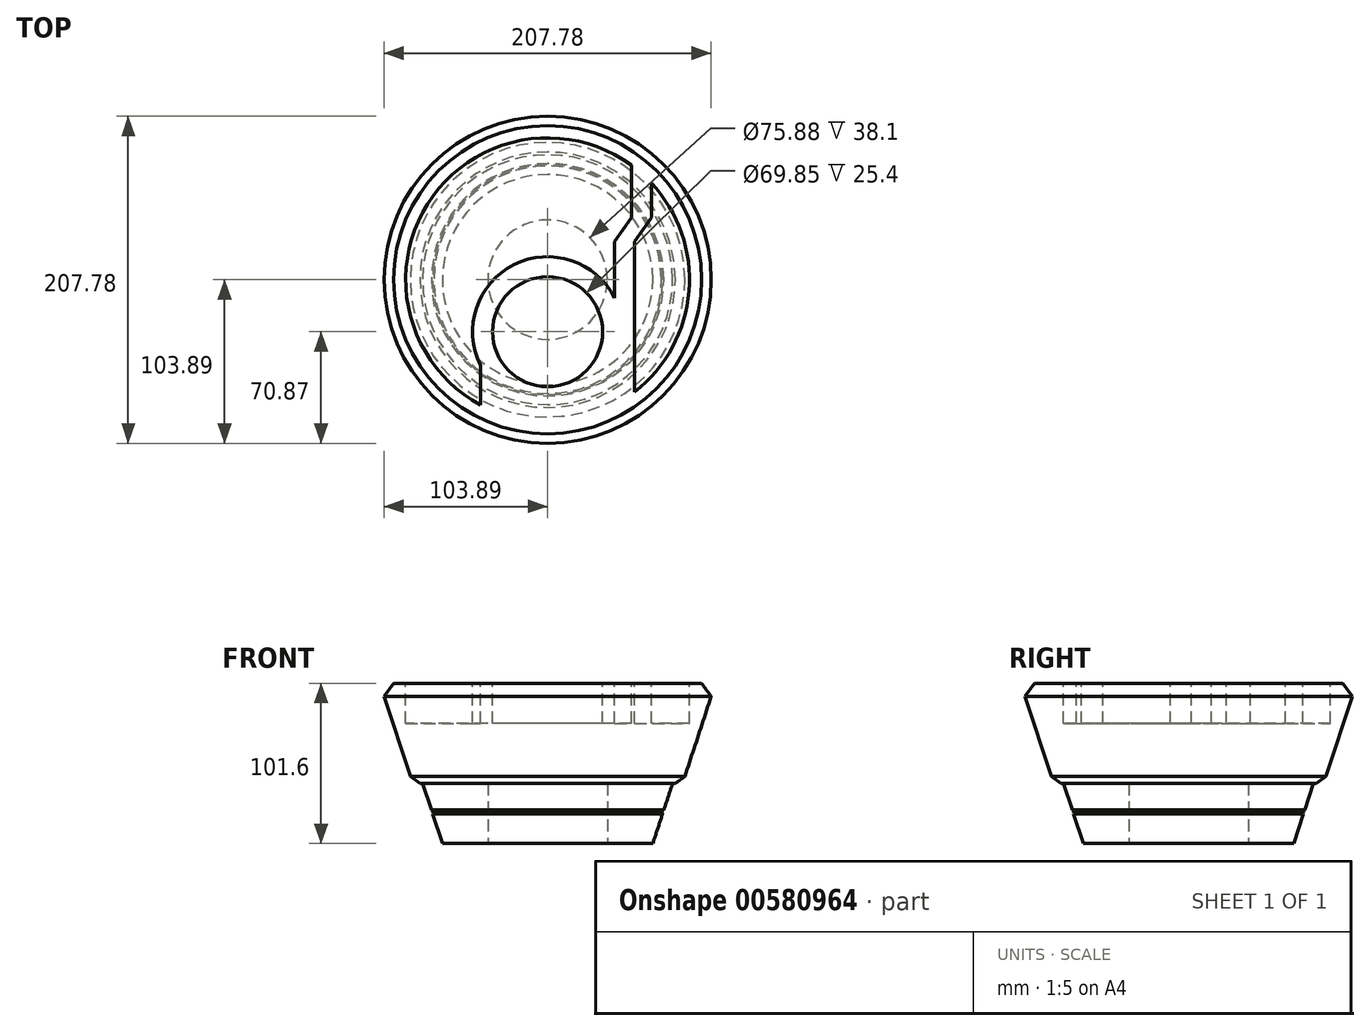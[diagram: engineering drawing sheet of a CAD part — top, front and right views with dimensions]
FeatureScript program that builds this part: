
annotation { "Feature Type Name" : "Feature", "Feature Type Description" : "" }
export const myFeature = defineFeature(function(context is Context, id is Id, definition is map)
    precondition{}
    {
        {
            var Q0;
            Q0=qCreatedBy(makeId("Top.planeOp"),FACE);
            var sketch = newSketch(context, id + "F0", { "sketchPlane" : qUnion([Q0])});
            skCircle(sketch, "E0", {"center": v(0, 0) * mm, "radius": 66.85 * mm});
            skSolve(sketch);
        }
        {
            var Q0;
            Q0=qCreatedBy(makeId("Top.planeOp"),FACE);
            cPlane(context, id + "F1", {"entities" : qUnion([Q0]), "cplaneType" : CPlaneType.OFFSET, "offset" : 101.6 * mm, "width" : 152.4 * mm, "height" : 152.4 * mm});
        }
        {
            var Q0;
            Q0=qCreatedBy(id+"F1.planeOp",FACE);
            var sketch = newSketch(context, id + "F2", { "sketchPlane" : qUnion([Q0])});
            skCircle(sketch, "E1", {"center": v(0, 0) * mm, "radius": 100.28 * mm});
            skSolve(sketch);
        }
        {
            var Q0;
            Q0=makeQuery(id+"F2.imprint","IMPRINT",FACE,{"disambiguationData":[TD([[makeQuery(id+"F2.imprint","IMPRINT",EDGE,{"derivedFrom":sQuery(id+"F2.wireOp",EDGE,"E1")}),1.0]])]});
            var Q1;
            Q1=makeQuery(id+"F0.imprint","IMPRINT",FACE,{"disambiguationData":[TD([[makeQuery(id+"F0.imprint","IMPRINT",EDGE,{"derivedFrom":sQuery(id+"F0.wireOp",EDGE,"E0")}),1.0]])]});
            var Q2;
            Q2=sQuery(id+"F2.wireOp",EDGE,"Eyu8YDiN-lEGU-Wuxt-0ncA-RZLAWeJK4OgB");
            var Q3;
            Q3=sQuery(id+"F0.wireOp",EDGE,"fgfE4CqQ-t5n6-ucAx-yhIW-5wF2yx0Jya2k");
            loft(context, id + "F3", {"sheetProfilesArray" : [{ "sheetProfileEntities" : qUnion([Q0]) }, { "sheetProfileEntities" : qUnion([Q1]) }], "wireProfilesArray" : [{ "wireProfileEntities" : qUnion([Q2]) }, { "wireProfileEntities" : qUnion([Q3]) }]});
        }
        {
            var Q0;
            Q0=qCreatedBy(makeId("Top.planeOp"),FACE);
            var sketch = newSketch(context, id + "F4", { "sketchPlane" : qUnion([Q0])});
            skCircle(sketch, "E2", {"center": v(0, 0) * mm, "radius": 37.94 * mm});
            skSolve(sketch);
        }
        {
            var Q0;
            Q0=makeQuery(id+"F4.imprint","IMPRINT",FACE,{"disambiguationData":[TD([[makeQuery(id+"F4.imprint","IMPRINT",EDGE,{"derivedFrom":sQuery(id+"F4.wireOp",EDGE,"E2")}),1.0]])]});
            extrude(context, id + "F5", {"entities" : qUnion([Q0]), "operationType" : NewBodyOperationType.REMOVE, "depth" : 53.34 * mm, "offsetDistance" : 25.4 * mm});
        }
        {
            var Q0;
            Q0=qCreatedBy(makeId("Top.planeOp"),FACE);
            cPlane(context, id + "F6", {"entities" : qUnion([Q0]), "cplaneType" : CPlaneType.OFFSET, "offset" : 38.1 * mm, "width" : 152.4 * mm, "height" : 152.4 * mm});
        }
        {
            var Q0;
            Q0=qCreatedBy(id+"F6.planeOp",FACE);
            var sketch = newSketch(context, id + "F7", { "sketchPlane" : qUnion([Q0])});
            skCircle(sketch, "E3", {"center": v(0, 0) * mm, "radius": 85.73 * mm});
            skSolve(sketch);
        }
        {
            var Q0;
            Q0=qCreatedBy(id+"F1.planeOp",FACE);
            var sketch = newSketch(context, id + "F8", { "sketchPlane" : qUnion([Q0])});
            skCircle(sketch, "E4", {"center": v(0, 0) * mm, "radius": 106.63 * mm});
            skSolve(sketch);
        }
        {
            var Q1;
            Q1=makeQuery(id+"F7.imprint","IMPRINT",FACE,{"disambiguationData":[TD([[makeQuery(id+"F7.imprint","IMPRINT",EDGE,{"derivedFrom":sQuery(id+"F7.wireOp",EDGE,"E3")}),1.0]])]});
            var Q2;
            Q2=makeQuery(id+"F8.imprint","IMPRINT",FACE,{"disambiguationData":[TD([[makeQuery(id+"F8.imprint","IMPRINT",EDGE,{"derivedFrom":sQuery(id+"F8.wireOp",EDGE,"E4")}),1.0]])]});
            loft(context, id + "F9", {"operationType" : NewBodyOperationType.ADD, "sheetProfilesArray" : [{ "sheetProfileEntities" : qUnion([Q1]) }, { "sheetProfileEntities" : qUnion([Q2]) }]});
        }
        {
            var Q0;
            Q0=makeQuery(id+"F9.opLoft","MID_CAP_EDGE",EDGE,{"disambiguationData":[OSD([sQuery(id+"F7.wireOp",EDGE,"E3")])],"capPos":0.0});
            chamfer(context, id + "F10", {"entities" : qUnion([Q0]), "width" : 6.35 * mm, "tangentPropagation" : true});
        }
        {
            var Q0;
            Q0=makeQuery(id+"F9.opLoft","MID_CAP_EDGE",EDGE,{"disambiguationData":[OSD([sQuery(id+"F7.wireOp",EDGE,"E3"),sQuery(id+"F8.wireOp",EDGE,"E4")])],"capPos":1.0});
            chamfer(context, id + "F11", {"entities" : qUnion([Q0]), "width" : 6.35 * mm, "tangentPropagation" : true});
        }
        {
            var Q0;
            Q0=qCreatedBy(makeId("Front.planeOp"),FACE);
            var sketch = newSketch(context, id + "F12", { "sketchPlane" : qUnion([Q0])});
            skLineSegment(sketch, "E5", {"start": v(-79.4, 38.11) * mm, "end": v(-66.85, 0) * mm});
            skLineSegment(sketch, "E6", {"start": v(-73.8, 21.14) * mm, "end": v(-72.2, 20.33) * mm});
            skLineSegment(sketch, "E7", {"start": v(-72.2, 20.33) * mm, "end": v(-73.02, 18.73) * mm});
            skSolve(sketch);
        }
        {
            var Q0;
            Q0=qCreatedBy(makeId("Right.planeOp"),FACE);
            var sketch = newSketch(context, id + "F13", { "sketchPlane" : qUnion([Q0])});
            skLineSegment(sketch, "E8", {"start": v(0, 0) * mm, "end": v(0, 184.2) * mm});
            skSolve(sketch);
        }
        {
            var Q0;
            Q0=qSketchRegion(id+"F12",true);
            var Q1;
            Q1=sQuery(id+"F13.wireOp",EDGE,"E8");
            revolve(context, id + "F14", {"operationType" : NewBodyOperationType.REMOVE, "entities" : qUnion([Q0]), "axis" : qUnion([Q1]), "revolveType" : RevolveType.FULL, "oppositeDirection" : true});
        }
        {
            var Q0;
            Q0=makeQuery(id+"F9.boolean.opBoolean","MERGE",FACE,{"derivedFrom":[makeQuery(id+"F3.opLoft","CAP_FACE",FACE,{"disambiguationData":[OSD([makeQuery(id+"F2.imprint","IMPRINT",FACE,{"disambiguationData":[TD([[makeQuery(id+"F2.imprint","IMPRINT",EDGE,{"derivedFrom":sQuery(id+"F2.wireOp",EDGE,"E1")}),1.0]])]})])],"isStart":true}),makeQuery(id+"F9.opLoft","CAP_FACE",FACE,{"disambiguationData":[OSD([makeQuery(id+"F8.imprint","IMPRINT",FACE,{"disambiguationData":[TD([[makeQuery(id+"F8.imprint","IMPRINT",EDGE,{"derivedFrom":sQuery(id+"F8.wireOp",EDGE,"E4")}),1.0]])]})])],"isStart":true})]});
            var sketch = newSketch(context, id + "F15", { "sketchPlane" : qUnion([Q0])});
            skCircle(sketch, "E9", {"center": v(0, -33.02) * mm, "radius": 47.63 * mm});
            skCircle(sketch, "E10", {"center": v(0, -33.02) * mm, "radius": 34.93 * mm});
            skLineSegment(sketch, "E11", {"start": v(-42.55, -90.8) * mm, "end": v(-42.55, 24.13) * mm});
            skLineSegment(sketch, "E12", {"start": v(-55.25, -83.7) * mm, "end": v(-55.25, 24.13) * mm});
            skLineSegment(sketch, "E13", {"start": v(-55.25, 24.13) * mm, "end": v(-65.92, 39.37) * mm});
            skLineSegment(sketch, "E14", {"start": v(-42.55, 24.13) * mm, "end": v(-53.22, 39.37) * mm});
            skLineSegment(sketch, "E15", {"start": v(-65.92, 39.37) * mm, "end": v(-65.92, 75.57) * mm});
            skLineSegment(sketch, "E16", {"start": v(-53.22, 39.37) * mm, "end": v(-53.22, 85) * mm});
            skLineSegment(sketch, "E17", {"start": v(0, -33.02) * mm, "end": v(11.18, -33.02) * mm});
            skLineSegment(sketch, "E18", {"start": v(0, -33.02) * mm, "end": v(0, -27.7) * mm});
            skLineSegment(sketch, "E19.MirrorCS", {"start": v(55.25, -83.7) * mm, "end": v(55.25, 24.13) * mm});
            skLineSegment(sketch, "E20.MirrorCS", {"start": v(42.55, -90.8) * mm, "end": v(42.55, 24.13) * mm});
            skLineSegment(sketch, "E21.MirrorCS", {"start": v(42.55, 24.13) * mm, "end": v(53.22, 39.37) * mm});
            skLineSegment(sketch, "E22.MirrorCS", {"start": v(55.25, 24.13) * mm, "end": v(65.92, 39.37) * mm});
            skLineSegment(sketch, "E23.MirrorCS", {"start": v(65.92, 39.37) * mm, "end": v(65.92, 75.57) * mm});
            skLineSegment(sketch, "E24.MirrorCS", {"start": v(53.22, 39.37) * mm, "end": v(53.22, 85) * mm});
            skCircle(sketch, "E25", {"center": v(0, 0) * mm, "radius": 90.12 * mm});
            skCircle(sketch, "E26", {"center": v(0, 0) * mm, "radius": 100.28 * mm});
            skSolve(sketch);
        }
        {
            var Q0;
            {var subQ0=sQuery(id+"F15.wireOp",EDGE,"E13");Q0=makeQuery(id+"F15.imprint","IMPRINT",FACE,{"disambiguationData":[TD([[makeQuery(id+"F15.imprint","IMPRINT",EDGE,{"derivedFrom":subQ0}),1.0]])]});}
            var Q1;
            {var subQ0=sQuery(id+"F15.wireOp",EDGE,"E14");Q1=makeQuery(id+"F15.imprint","IMPRINT",FACE,{"disambiguationData":[TD([[makeQuery(id+"F15.imprint","IMPRINT",EDGE,{"derivedFrom":subQ0}),-1.0]])]});}
            var Q2;
            Q2=makeQuery(id+"F15.imprint","IMPRINT",FACE,{"disambiguationData":[TD([[makeQuery(id+"F15.imprint","IMPRINT",EDGE,{"derivedFrom":sQuery(id+"F15.wireOp",EDGE,"E10")}),1.0]])]});
            var Q3;
            {var subQ0=sQuery(id+"F15.wireOp",EDGE,"E11");var subQ1=sQuery(id+"F15.wireOp",EDGE,"E9");var subQ2=makeQuery(id+"F15.imprint","INTERSECT",VERTEX,{"disambiguationData":[OD(1.0)],"derivedFrom":[subQ1,subQ0]});Q3=makeQuery(id+"F15.imprint","IMPRINT",FACE,{"disambiguationData":[TD([[makeQuery(id+"F15.imprint","IMPRINT",EDGE,{"disambiguationData":[TD([[subQ2,-1.0]])],"derivedFrom":subQ1}),-1.0]])]});}
            var Q4;
            {var subQ0=sQuery(id+"F15.wireOp",EDGE,"E22.MirrorCS");Q4=makeQuery(id+"F15.imprint","IMPRINT",FACE,{"disambiguationData":[TD([[makeQuery(id+"F15.imprint","IMPRINT",EDGE,{"derivedFrom":subQ0}),-1.0]])]});}
            extrude(context, id + "F16", {"entities" : qUnion([Q0, Q1, Q2, Q3, Q4]), "operationType" : NewBodyOperationType.REMOVE, "oppositeDirection" : true, "depth" : 25.4 * mm, "offsetDistance" : 25.4 * mm});
        }
    });
